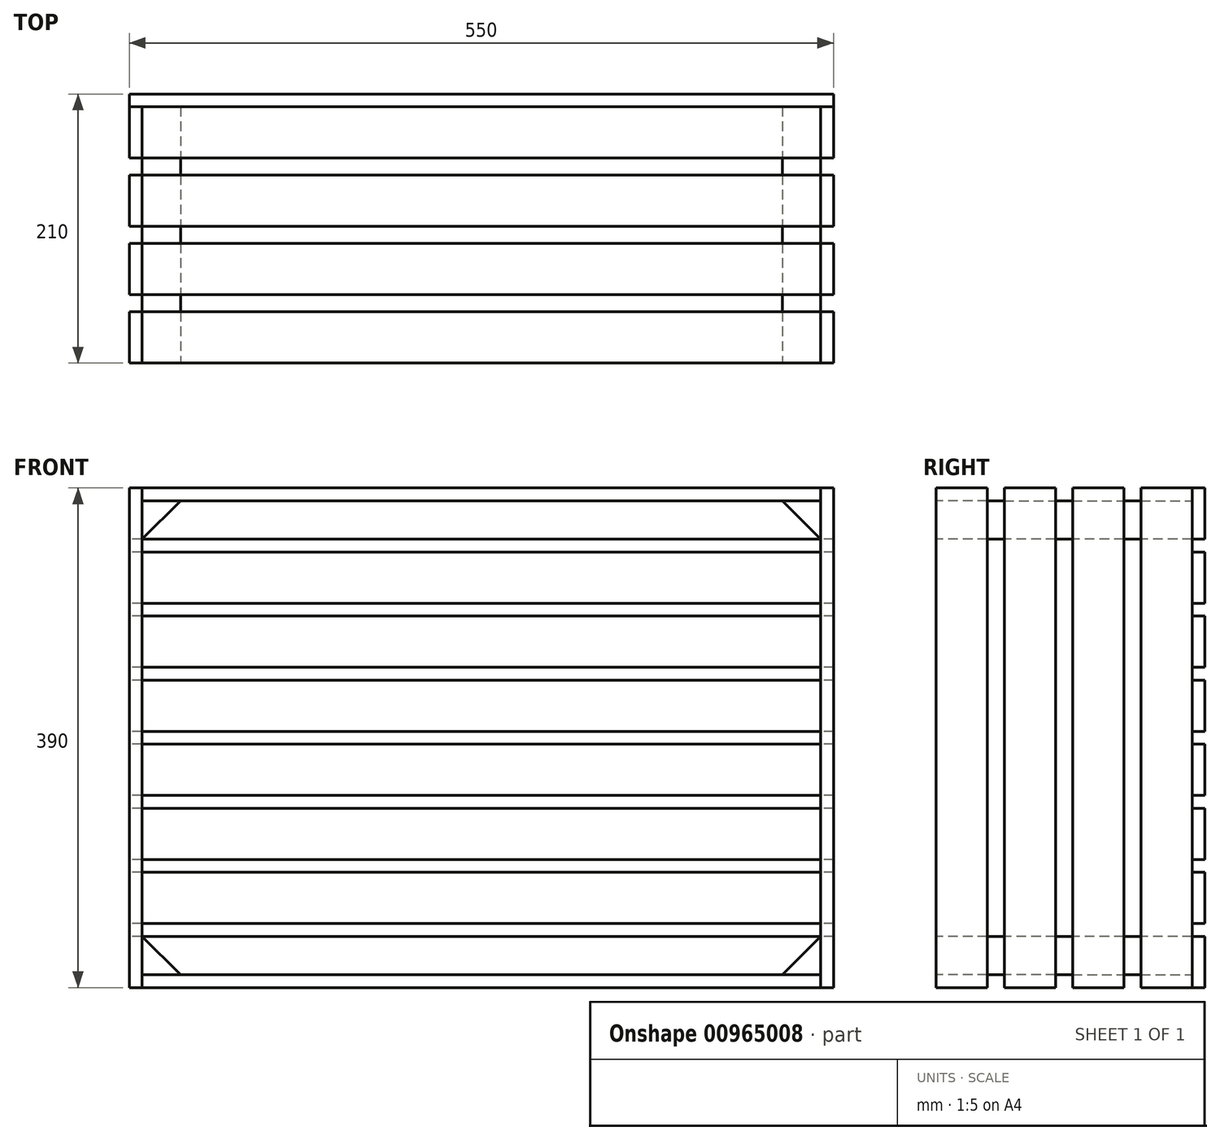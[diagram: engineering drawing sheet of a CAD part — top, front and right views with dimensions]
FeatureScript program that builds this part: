
annotation { "Feature Type Name" : "Feature", "Feature Type Description" : "" }
export const myFeature = defineFeature(function(context is Context, id is Id, definition is map)
    precondition{}
    {
        {
            assignVariable(context, id + "F0", {"variableType" : VariableType.LENGTH, "name" : "sirinaLetvice", "lengthValue" : 40 * mm});
        }
        {
            assignVariable(context, id + "F1", {"variableType" : VariableType.LENGTH, "name" : "debelinaDeske", "lengthValue" : 10 * mm});
        }
        {
            assignVariable(context, id + "F2", {"variableType" : VariableType.LENGTH, "name" : "globina", "lengthValue" : 200 * mm});
        }
        {
            var Q0;
            Q0=qCreatedBy(makeId("Front.planeOp"),FACE);
            var sketch = newSketch(context, id + "F3", { "sketchPlane" : qUnion([Q0])});
            skLineSegment(sketch, "E0.bottom", {"start": v(-275, 195) * mm, "end": v(275, 195) * mm});
            skLineSegment(sketch, "E0.top", {"start": v(-275, -195) * mm, "end": v(275, -195) * mm});
            skLineSegment(sketch, "E0.left", {"start": v(-275, 195) * mm, "end": v(-275, -195) * mm});
            skLineSegment(sketch, "E0.right", {"start": v(275, 195) * mm, "end": v(275, -195) * mm});
            skPoint(sketch, "E0.middle", {"position": v(0, 0) * mm});
            skLineSegment(sketch, "E1", {"start": v(-265, 185) * mm, "end": v(265, 185) * mm});
            skLineSegment(sketch, "E2", {"start": v(-265, -185) * mm, "end": v(265, -185) * mm});
            skPoint(sketch, "E3.bottom.start.orphan", {"position": v(-265, 195) * mm});
            skLineSegment(sketch, "E4", {"start": v(-265, 185) * mm, "end": v(-265, -185) * mm});
            skLineSegment(sketch, "E5", {"start": v(265, 185) * mm, "end": v(265, -185) * mm});
            skLineSegment(sketch, "E6", {"start": v(-235, 185) * mm, "end": v(-265, 155) * mm});
            skLineSegment(sketch, "E7", {"start": v(235, 185) * mm, "end": v(265, 155) * mm});
            skLineSegment(sketch, "E8", {"start": v(265, -155) * mm, "end": v(235, -185) * mm});
            skLineSegment(sketch, "E9", {"start": v(-235, -185) * mm, "end": v(-265, -155) * mm});
            skLineSegment(sketch, "E10", {"start": v(-265, 195) * mm, "end": v(-265, 185) * mm});
            skLineSegment(sketch, "E11", {"start": v(-265, -185) * mm, "end": v(-265, -195) * mm});
            skLineSegment(sketch, "E12", {"start": v(265, 185) * mm, "end": v(265, 195) * mm});
            skLineSegment(sketch, "E13", {"start": v(265, -185) * mm, "end": v(265, -195) * mm});
            skSolve(sketch);
        }
        {
            var Q0;
            {var subQ4=sQuery(id+"F3.wireOp",EDGE,"E0.left");Q0=makeQuery(id+"F3.imprint","IMPRINT",FACE,{"disambiguationData":[TD([[makeQuery(id+"F3.imprint","IMPRINT",EDGE,{"derivedFrom":subQ4}),1.0]])]});}
            var Q1;
            {var subQ3=sQuery(id+"F3.wireOp",EDGE,"E0.right");Q1=makeQuery(id+"F3.imprint","IMPRINT",FACE,{"disambiguationData":[TD([[makeQuery(id+"F3.imprint","IMPRINT",EDGE,{"derivedFrom":subQ3}),-1.0]])]});}
            var Q2;
            {var subQ4=sQuery(id+"F3.wireOp",EDGE,"E0.left");Q2=makeQuery(id+"F3.imprint","IMPRINT",FACE,{"disambiguationData":[TD([[makeQuery(id+"F3.imprint","IMPRINT",EDGE,{"derivedFrom":subQ4}),1.0]])]});}
            var Q3;
            {var subQ3=sQuery(id+"F3.wireOp",EDGE,"E0.right");Q3=makeQuery(id+"F3.imprint","IMPRINT",FACE,{"disambiguationData":[TD([[makeQuery(id+"F3.imprint","IMPRINT",EDGE,{"derivedFrom":subQ3}),-1.0]])]});}
            var Q4;
            {var subQ4=sQuery(id+"F3.wireOp",EDGE,"E0.left");Q4=makeQuery(id+"F3.imprint","IMPRINT",FACE,{"disambiguationData":[TD([[makeQuery(id+"F3.imprint","IMPRINT",EDGE,{"derivedFrom":subQ4}),1.0]])]});}
            var Q5;
            {var subQ3=sQuery(id+"F3.wireOp",EDGE,"E0.right");Q5=makeQuery(id+"F3.imprint","IMPRINT",FACE,{"disambiguationData":[TD([[makeQuery(id+"F3.imprint","IMPRINT",EDGE,{"derivedFrom":subQ3}),-1.0]])]});}
            extrude(context, id + "F4", {"entities" : qUnion([Q0, Q1, Q2, Q3, Q4, Q5]), "oppositeDirection" : true, "depth" : getVariable(context, 'sirinaLetvice'), "offsetDistance" : 25 * mm});
        }
        {
            var Q0;
            {var subQ0=sQuery(id+"F3.wireOp",EDGE,"E6");Q0=makeQuery(id+"F3.imprint","IMPRINT",FACE,{"disambiguationData":[TD([[makeQuery(id+"F3.imprint","IMPRINT",EDGE,{"derivedFrom":subQ0}),-1.0]])]});}
            var Q1;
            {var subQ3=sQuery(id+"F3.wireOp",EDGE,"E7");Q1=makeQuery(id+"F3.imprint","IMPRINT",FACE,{"disambiguationData":[TD([[makeQuery(id+"F3.imprint","IMPRINT",EDGE,{"derivedFrom":subQ3}),1.0]])]});}
            var Q2;
            {var subQ0=sQuery(id+"F3.wireOp",EDGE,"E8");Q2=makeQuery(id+"F3.imprint","IMPRINT",FACE,{"disambiguationData":[TD([[makeQuery(id+"F3.imprint","IMPRINT",EDGE,{"derivedFrom":subQ0}),1.0]])]});}
            var Q3;
            {var subQ0=sQuery(id+"F3.wireOp",EDGE,"E9");Q3=makeQuery(id+"F3.imprint","IMPRINT",FACE,{"disambiguationData":[TD([[makeQuery(id+"F3.imprint","IMPRINT",EDGE,{"derivedFrom":subQ0}),1.0]])]});}
            extrude(context, id + "F5", {"entities" : qUnion([Q0, Q1, Q2, Q3]), "oppositeDirection" : true, "depth" : getVariable(context, 'globina'), "offsetDistance" : 25 * mm});
        }
        {
            var Q0;
            {var subQ2=sQuery(id+"F3.wireOp",EDGE,"E10");Q0=makeQuery(id+"F3.imprint","IMPRINT",FACE,{"disambiguationData":[TD([[makeQuery(id+"F3.imprint","IMPRINT",EDGE,{"derivedFrom":subQ2}),1.0]])]});}
            var Q1;
            {var subQ4=sQuery(id+"F3.wireOp",EDGE,"E11");Q1=makeQuery(id+"F3.imprint","IMPRINT",FACE,{"disambiguationData":[TD([[makeQuery(id+"F3.imprint","IMPRINT",EDGE,{"derivedFrom":subQ4}),1.0]])]});}
            extrude(context, id + "F6", {"entities" : qUnion([Q0, Q1]), "oppositeDirection" : true, "depth" : getVariable(context, 'sirinaLetvice'), "offsetDistance" : 25 * mm});
        }
        {
            var Q0;
            Q0=makeQuery(id+"F4.opExtrude","SWEPT_FACE",FACE,{"disambiguationData":[OSD([sQuery(id+"F3.wireOp",EDGE,"E0.right")])]});
            var sketch = newSketch(context, id + "F7", { "sketchPlane" : qUnion([Q0])});
            skLineSegment(sketch, "E14", {"start": v(200, 195) * mm, "end": v(200, -195) * mm, "construction": true});
            skLineSegment(sketch, "E15.top", {"start": v(53.33, -195) * mm, "end": v(93.33, -195) * mm});
            skLineSegment(sketch, "E15.left", {"start": v(53.33, 195) * mm, "end": v(53.33, -195) * mm});
            skLineSegment(sketch, "E15.right", {"start": v(93.33, 195) * mm, "end": v(93.33, -195) * mm});
            skLineSegment(sketch, "E16", {"start": v(53.33, 195) * mm, "end": v(93.33, 195) * mm});
            skLineSegment(sketch, "E17.bottom", {"start": v(106.67, 195) * mm, "end": v(146.67, 195) * mm});
            skLineSegment(sketch, "E17.top", {"start": v(106.67, -195) * mm, "end": v(146.67, -195) * mm});
            skLineSegment(sketch, "E17.left", {"start": v(106.67, 195) * mm, "end": v(106.67, -195) * mm});
            skLineSegment(sketch, "E17.right", {"start": v(146.67, 195) * mm, "end": v(146.67, -195) * mm});
            skLineSegment(sketch, "E18.bottom", {"start": v(160, 195) * mm, "end": v(200, 195) * mm});
            skLineSegment(sketch, "E18.top", {"start": v(160, -195) * mm, "end": v(200, -195) * mm});
            skLineSegment(sketch, "E18.left", {"start": v(160, 195) * mm, "end": v(160, -195) * mm});
            skLineSegment(sketch, "E18.right", {"start": v(200, 195) * mm, "end": v(200, -195) * mm});
            skSolve(sketch);
        }
        {
            var Q0;
            Q0=makeQuery(id+"F7.imprint","IMPRINT",FACE,{"disambiguationData":[TD([[makeQuery(id+"F7.imprint","IMPRINT",EDGE,{"derivedFrom":sQuery(id+"F7.wireOp",EDGE,"E15.top")}),1.0]])]});
            var Q1;
            Q1=makeQuery(id+"F7.imprint","IMPRINT",FACE,{"disambiguationData":[TD([[makeQuery(id+"F7.imprint","IMPRINT",EDGE,{"derivedFrom":sQuery(id+"F7.wireOp",EDGE,"E17.bottom")}),-1.0]])]});
            var Q2;
            Q2=makeQuery(id+"F7.imprint","IMPRINT",FACE,{"disambiguationData":[TD([[makeQuery(id+"F7.imprint","IMPRINT",EDGE,{"derivedFrom":sQuery(id+"F7.wireOp",EDGE,"E18.bottom")}),-1.0]])]});
            var Q3;
            {var subQ0=sQuery(id+"F3.wireOp",EDGE,"E5");Q3=makeQuery(id+"F5.opExtrude","SWEPT_FACE",FACE,{"disambiguationData":[OSD([subQ0]),TDD([makeQuery(id+"F3.imprint","IMPRINT",EDGE,{"disambiguationData":[TD([[makeQuery(id+"F3.imprint","INTERSECT",VERTEX,{"derivedFrom":[subQ0,sQuery(id+"F3.wireOp",EDGE,"E7")]}),1.0]])],"derivedFrom":subQ0})])]});}
            extrude(context, id + "F8", {"entities" : qUnion([Q0, Q1, Q2]), "endBound" : BoundingType.UP_TO_SURFACE, "oppositeDirection" : true, "depth" : 25 * mm, "endBoundEntityFace" : qUnion([Q3]), "offsetDistance" : 25 * mm});
        }
        {
            var Q0;
            Q0=makeQuery(id+"F8.opExtrude","SWEPT_BODY",BODY,{"disambiguationData":[OSD([sQuery(id+"F7.wireOp",EDGE,"E15.top"),sQuery(id+"F7.wireOp",EDGE,"E15.left"),sQuery(id+"F7.wireOp",EDGE,"E15.right"),sQuery(id+"F7.wireOp",EDGE,"E16")])]});
            var Q1;
            Q1=makeQuery(id+"F8.opExtrude","SWEPT_BODY",BODY,{"disambiguationData":[OSD([sQuery(id+"F7.wireOp",EDGE,"E17.bottom"),sQuery(id+"F7.wireOp",EDGE,"E17.top"),sQuery(id+"F7.wireOp",EDGE,"E17.left"),sQuery(id+"F7.wireOp",EDGE,"E17.right")])]});
            var Q2;
            Q2=makeQuery(id+"F8.opExtrude","SWEPT_BODY",BODY,{"disambiguationData":[OSD([sQuery(id+"F7.wireOp",EDGE,"E18.bottom"),sQuery(id+"F7.wireOp",EDGE,"E18.top"),sQuery(id+"F7.wireOp",EDGE,"E18.left"),sQuery(id+"F7.wireOp",EDGE,"E18.right")])]});
            var Q3;
            Q3=qCreatedBy(makeId("Right.planeOp"),FACE);
            mirror(context, id + "F9", {"entities" : qUnion([Q0, Q1, Q2]), "mirrorPlane" : qUnion([Q3])});
        }
        {
            var Q0;
            Q0=makeQuery(id+"F6.opExtrude","SWEPT_FACE",FACE,{"disambiguationData":[OSD([sQuery(id+"F3.wireOp",EDGE,"E0.bottom")])]});
            var sketch = newSketch(context, id + "F10", { "sketchPlane" : qUnion([Q0])});
            skLineSegment(sketch, "E19.bottom", {"start": v(265, 53.33) * mm, "end": v(-265, 53.33) * mm});
            skLineSegment(sketch, "E19.top", {"start": v(265, 93.33) * mm, "end": v(-265, 93.33) * mm});
            skLineSegment(sketch, "E19.left", {"start": v(265, 53.33) * mm, "end": v(265, 93.33) * mm});
            skLineSegment(sketch, "E19.right", {"start": v(-265, 53.33) * mm, "end": v(-265, 93.33) * mm});
            skLineSegment(sketch, "E20.bottom", {"start": v(265, 106.67) * mm, "end": v(-265, 106.67) * mm});
            skLineSegment(sketch, "E20.top", {"start": v(265, 146.67) * mm, "end": v(-265, 146.67) * mm});
            skLineSegment(sketch, "E20.left", {"start": v(265, 106.67) * mm, "end": v(265, 146.67) * mm});
            skLineSegment(sketch, "E20.right", {"start": v(-265, 106.67) * mm, "end": v(-265, 146.67) * mm});
            skLineSegment(sketch, "E21.bottom", {"start": v(265, 160) * mm, "end": v(-265, 160) * mm});
            skLineSegment(sketch, "E21.top", {"start": v(265, 200) * mm, "end": v(-265, 200) * mm});
            skLineSegment(sketch, "E21.left", {"start": v(265, 160) * mm, "end": v(265, 200) * mm});
            skLineSegment(sketch, "E21.right", {"start": v(-265, 160) * mm, "end": v(-265, 200) * mm});
            skSolve(sketch);
        }
        {
            var Q0;
            Q0=makeQuery(id+"F10.imprint","IMPRINT",FACE,{"disambiguationData":[TD([[makeQuery(id+"F10.imprint","IMPRINT",EDGE,{"derivedFrom":sQuery(id+"F10.wireOp",EDGE,"E19.bottom")}),-1.0]])]});
            var Q1;
            Q1=makeQuery(id+"F10.imprint","IMPRINT",FACE,{"disambiguationData":[TD([[makeQuery(id+"F10.imprint","IMPRINT",EDGE,{"derivedFrom":sQuery(id+"F10.wireOp",EDGE,"E20.bottom")}),-1.0]])]});
            var Q2;
            Q2=makeQuery(id+"F10.imprint","IMPRINT",FACE,{"disambiguationData":[TD([[makeQuery(id+"F10.imprint","IMPRINT",EDGE,{"derivedFrom":sQuery(id+"F10.wireOp",EDGE,"E21.bottom")}),-1.0]])]});
            var Q3;
            {var subQ0=sQuery(id+"F3.wireOp",EDGE,"E1");Q3=makeQuery(id+"F5.opExtrude","SWEPT_FACE",FACE,{"disambiguationData":[OSD([subQ0]),TDD([makeQuery(id+"F3.imprint","IMPRINT",EDGE,{"disambiguationData":[TD([[makeQuery(id+"F3.imprint","INTERSECT",VERTEX,{"derivedFrom":[subQ0,sQuery(id+"F3.wireOp",EDGE,"E7")]}),-1.0]])],"derivedFrom":subQ0})])]});}
            extrude(context, id + "F11", {"entities" : qUnion([Q0, Q1, Q2]), "endBound" : BoundingType.UP_TO_SURFACE, "oppositeDirection" : true, "depth" : 25 * mm, "endBoundEntityFace" : qUnion([Q3]), "offsetDistance" : 25 * mm});
        }
        {
            var Q0;
            Q0=makeQuery(id+"F11.opExtrude","SWEPT_BODY",BODY,{"disambiguationData":[OSD([sQuery(id+"F10.wireOp",EDGE,"E19.bottom"),sQuery(id+"F10.wireOp",EDGE,"E19.top"),sQuery(id+"F10.wireOp",EDGE,"E19.left"),sQuery(id+"F10.wireOp",EDGE,"E19.right")])]});
            var Q1;
            Q1=makeQuery(id+"F11.opExtrude","SWEPT_BODY",BODY,{"disambiguationData":[OSD([sQuery(id+"F10.wireOp",EDGE,"E20.bottom"),sQuery(id+"F10.wireOp",EDGE,"E20.top"),sQuery(id+"F10.wireOp",EDGE,"E20.left"),sQuery(id+"F10.wireOp",EDGE,"E20.right")])]});
            var Q2;
            Q2=makeQuery(id+"F11.opExtrude","SWEPT_BODY",BODY,{"disambiguationData":[OSD([sQuery(id+"F10.wireOp",EDGE,"E21.bottom"),sQuery(id+"F10.wireOp",EDGE,"E21.top"),sQuery(id+"F10.wireOp",EDGE,"E21.left"),sQuery(id+"F10.wireOp",EDGE,"E21.right")])]});
            var Q3;
            Q3=qCreatedBy(makeId("Top.planeOp"),FACE);
            mirror(context, id + "F12", {"entities" : qUnion([Q0, Q1, Q2]), "mirrorPlane" : qUnion([Q3])});
        }
        {
            var Q0;
            Q0=makeQuery(id+"F11.opExtrude","SWEPT_FACE",FACE,{"disambiguationData":[OSD([sQuery(id+"F10.wireOp",EDGE,"E21.top")])]});
            var sketch = newSketch(context, id + "F13", { "sketchPlane" : qUnion([Q0])});
            skLineSegment(sketch, "E22.bottom", {"start": v(-275, 195) * mm, "end": v(275, 195) * mm});
            skLineSegment(sketch, "E22.top", {"start": v(-275, 155) * mm, "end": v(275, 155) * mm});
            skLineSegment(sketch, "E22.left", {"start": v(-275, 195) * mm, "end": v(-275, 155) * mm});
            skLineSegment(sketch, "E22.right", {"start": v(275, 195) * mm, "end": v(275, 155) * mm});
            skLineSegment(sketch, "E23.bottom", {"start": v(-275, 145) * mm, "end": v(275, 145) * mm});
            skLineSegment(sketch, "E23.top", {"start": v(-275, 105) * mm, "end": v(275, 105) * mm});
            skLineSegment(sketch, "E23.left", {"start": v(-275, 145) * mm, "end": v(-275, 105) * mm});
            skLineSegment(sketch, "E23.right", {"start": v(275, 145) * mm, "end": v(275, 105) * mm});
            skLineSegment(sketch, "E24.bottom", {"start": v(-275, 95) * mm, "end": v(275, 95) * mm});
            skLineSegment(sketch, "E24.top", {"start": v(-275, 55) * mm, "end": v(275, 55) * mm});
            skLineSegment(sketch, "E24.left", {"start": v(-275, 95) * mm, "end": v(-275, 55) * mm});
            skLineSegment(sketch, "E24.right", {"start": v(275, 95) * mm, "end": v(275, 55) * mm});
            skLineSegment(sketch, "E25.bottom", {"start": v(-275, 45) * mm, "end": v(275, 45) * mm});
            skLineSegment(sketch, "E25.top", {"start": v(-275, 5) * mm, "end": v(275, 5) * mm});
            skLineSegment(sketch, "E25.left", {"start": v(-275, 45) * mm, "end": v(-275, 5) * mm});
            skLineSegment(sketch, "E25.right", {"start": v(275, 45) * mm, "end": v(275, 5) * mm});
            skLineSegment(sketch, "E26.bottom", {"start": v(-275, -5) * mm, "end": v(275, -5) * mm});
            skLineSegment(sketch, "E26.top", {"start": v(-275, -45) * mm, "end": v(275, -45) * mm});
            skLineSegment(sketch, "E26.left", {"start": v(-275, -5) * mm, "end": v(-275, -45) * mm});
            skLineSegment(sketch, "E26.right", {"start": v(275, -5) * mm, "end": v(275, -45) * mm});
            skLineSegment(sketch, "E27.bottom", {"start": v(-275, -55) * mm, "end": v(275, -55) * mm});
            skLineSegment(sketch, "E27.top", {"start": v(-275, -95) * mm, "end": v(275, -95) * mm});
            skLineSegment(sketch, "E27.left", {"start": v(-275, -55) * mm, "end": v(-275, -95) * mm});
            skLineSegment(sketch, "E27.right", {"start": v(275, -55) * mm, "end": v(275, -95) * mm});
            skLineSegment(sketch, "E28.bottom", {"start": v(-275, -105) * mm, "end": v(275, -105) * mm});
            skLineSegment(sketch, "E28.top", {"start": v(-275, -145) * mm, "end": v(275, -145) * mm});
            skLineSegment(sketch, "E28.left", {"start": v(-275, -105) * mm, "end": v(-275, -145) * mm});
            skLineSegment(sketch, "E28.right", {"start": v(275, -105) * mm, "end": v(275, -145) * mm});
            skLineSegment(sketch, "E29.bottom", {"start": v(-275, -155) * mm, "end": v(275, -155) * mm});
            skLineSegment(sketch, "E29.top", {"start": v(-275, -195) * mm, "end": v(275, -195) * mm});
            skLineSegment(sketch, "E29.left", {"start": v(-275, -155) * mm, "end": v(-275, -195) * mm});
            skLineSegment(sketch, "E29.right", {"start": v(275, -155) * mm, "end": v(275, -195) * mm});
            skSolve(sketch);
        }
        {
            var Q0;
            Q0=makeQuery(id+"F13.imprint","IMPRINT",FACE,{"disambiguationData":[TD([[makeQuery(id+"F13.imprint","IMPRINT",EDGE,{"derivedFrom":sQuery(id+"F13.wireOp",EDGE,"E22.top")}),1.0]])]});
            var Q1;
            {var subQ1=sQuery(id+"F10.wireOp",EDGE,"E21.top");Q1=makeQuery(id+"F13.imprint","IMPRINT",FACE,{"disambiguationData":[TD([[makeQuery(id+"F13.imprint","IMPRINT",EDGE,{"derivedFrom":makeQuery(id+"F11.opExtrude","CAP_EDGE",EDGE,{"disambiguationData":[OSD([subQ1])],"isStart":false})}),1.0]])]});}
            extrude(context, id + "F14", {"entities" : qUnion([Q0, Q1]), "depth" : getVariable(context, 'debelinaDeske'), "offsetDistance" : 25 * mm});
        }
        {
            var Q0;
            Q0=makeQuery(id+"F13.imprint","IMPRINT",FACE,{"disambiguationData":[TD([[makeQuery(id+"F13.imprint","IMPRINT",EDGE,{"derivedFrom":sQuery(id+"F13.wireOp",EDGE,"E23.bottom")}),-1.0]])]});
            var Q1;
            Q1=makeQuery(id+"F13.imprint","IMPRINT",FACE,{"disambiguationData":[TD([[makeQuery(id+"F13.imprint","IMPRINT",EDGE,{"derivedFrom":sQuery(id+"F13.wireOp",EDGE,"E24.bottom")}),-1.0]])]});
            var Q2;
            Q2=makeQuery(id+"F13.imprint","IMPRINT",FACE,{"disambiguationData":[TD([[makeQuery(id+"F13.imprint","IMPRINT",EDGE,{"derivedFrom":sQuery(id+"F13.wireOp",EDGE,"E25.bottom")}),-1.0]])]});
            var Q3;
            Q3=makeQuery(id+"F13.imprint","IMPRINT",FACE,{"disambiguationData":[TD([[makeQuery(id+"F13.imprint","IMPRINT",EDGE,{"derivedFrom":sQuery(id+"F13.wireOp",EDGE,"E26.bottom")}),-1.0]])]});
            var Q4;
            Q4=makeQuery(id+"F13.imprint","IMPRINT",FACE,{"disambiguationData":[TD([[makeQuery(id+"F13.imprint","IMPRINT",EDGE,{"derivedFrom":sQuery(id+"F13.wireOp",EDGE,"E27.bottom")}),-1.0]])]});
            var Q5;
            Q5=makeQuery(id+"F13.imprint","IMPRINT",FACE,{"disambiguationData":[TD([[makeQuery(id+"F13.imprint","IMPRINT",EDGE,{"derivedFrom":sQuery(id+"F13.wireOp",EDGE,"E28.bottom")}),-1.0]])]});
            var Q6;
            Q6=makeQuery(id+"F13.imprint","IMPRINT",FACE,{"disambiguationData":[TD([[makeQuery(id+"F13.imprint","IMPRINT",EDGE,{"derivedFrom":sQuery(id+"F13.wireOp",EDGE,"E29.bottom")}),-1.0]])]});
            extrude(context, id + "F15", {"entities" : qUnion([Q0, Q1, Q2, Q3, Q4, Q5, Q6]), "depth" : getVariable(context, 'debelinaDeske'), "offsetDistance" : 25 * mm});
        }
    });
